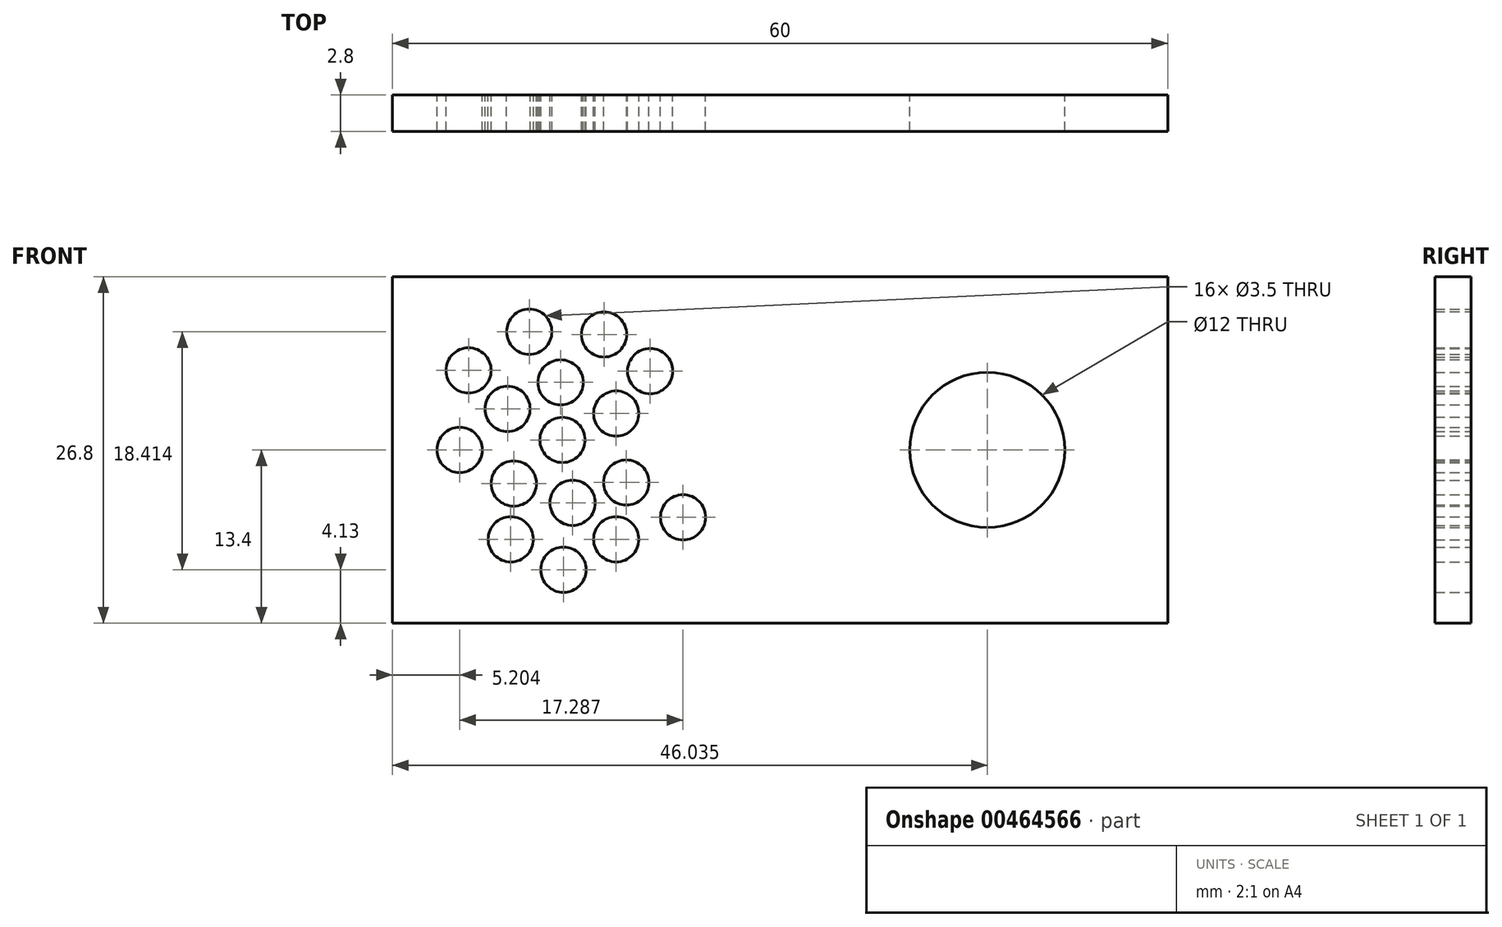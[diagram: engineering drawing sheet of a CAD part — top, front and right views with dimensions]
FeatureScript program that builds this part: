
annotation { "Feature Type Name" : "Feature", "Feature Type Description" : "" }
export const myFeature = defineFeature(function(context is Context, id is Id, definition is map)
    precondition{}
    {
        {
            var Q0;
            Q0=qCreatedBy(makeId("Front.planeOp"),FACE);
            var sketch = newSketch(context, id + "F0", { "sketchPlane" : qUnion([Q0])});
            skLineSegment(sketch, "E0.bottom", {"start": v(30, 13.4) * mm, "end": v(-30, 13.4) * mm});
            skLineSegment(sketch, "E0.top", {"start": v(30, -13.4) * mm, "end": v(-30, -13.4) * mm});
            skLineSegment(sketch, "E0.left", {"start": v(30, 13.4) * mm, "end": v(30, -13.4) * mm});
            skLineSegment(sketch, "E0.right", {"start": v(-30, 13.4) * mm, "end": v(-30, -13.4) * mm});
            skPoint(sketch, "E0.middle", {"position": v(0, 0) * mm});
            skSolve(sketch);
        }
        {
            var Q0;
            Q0 = qSketchRegion(id + "F0", true);
            extrude(context, id + "F1", {"entities" : qUnion([Q0]), "depth" : 2.8 * mm});
        }
        {
            var Q0;
            Q0=qCreatedBy(makeId("Front.planeOp"),FACE);
            var sketch = newSketch(context, id + "F2", { "sketchPlane" : qUnion([Q0])});
            skCircle(sketch, "E1", {"center": v(-19.4, 9.14) * mm, "radius": 1.75 * mm});
            skCircle(sketch, "E2", {"center": v(-21.09, 3.17) * mm, "radius": 1.75 * mm});
            skCircle(sketch, "E3", {"center": v(-16.98, 5.23) * mm, "radius": 1.75 * mm});
            skCircle(sketch, "E4", {"center": v(-16.84, 0.77) * mm, "radius": 1.75 * mm});
            skCircle(sketch, "E5", {"center": v(-20.6, -2.6) * mm, "radius": 1.75 * mm});
            skCircle(sketch, "E6", {"center": v(-16.06, -4.1) * mm, "radius": 1.75 * mm});
            skCircle(sketch, "E7", {"center": v(-13.62, 8.93) * mm, "radius": 1.75 * mm});
            skCircle(sketch, "E8", {"center": v(-12.68, 2.81) * mm, "radius": 1.75 * mm});
            skCircle(sketch, "E9", {"center": v(-11.9, -2.52) * mm, "radius": 1.75 * mm});
            skCircle(sketch, "E10", {"center": v(-12.68, -6.92) * mm, "radius": 1.75 * mm});
            skCircle(sketch, "E11", {"center": v(-20.84, -6.92) * mm, "radius": 1.75 * mm});
            skCircle(sketch, "E12", {"center": v(-16.76, -9.27) * mm, "radius": 1.75 * mm});
            skCircle(sketch, "E13", {"center": v(16.04, 0) * mm, "radius": 6 * mm});
            skCircle(sketch, "E14", {"center": v(-10.05, 6.1) * mm, "radius": 1.75 * mm});
            skCircle(sketch, "E15", {"center": v(-24.8, 0) * mm, "radius": 1.75 * mm});
            skCircle(sketch, "E16", {"center": v(-24.1, 6.15) * mm, "radius": 1.75 * mm});
            skCircle(sketch, "E17", {"center": v(-7.5, -5.21) * mm, "radius": 1.75 * mm});
            skSolve(sketch);
        }
        {
            var Q0;
            Q0 = qSketchRegion(id + "F2", true);
            extrude(context, id + "F3", {"entities" : qUnion([Q0]), "operationType" : NewBodyOperationType.REMOVE, "depth" : 25 * mm, "hasSecondDirection" : true, "secondDirectionOppositeDirection" : true, "secondDirectionDepth" : 25 * mm});
        }
    });
